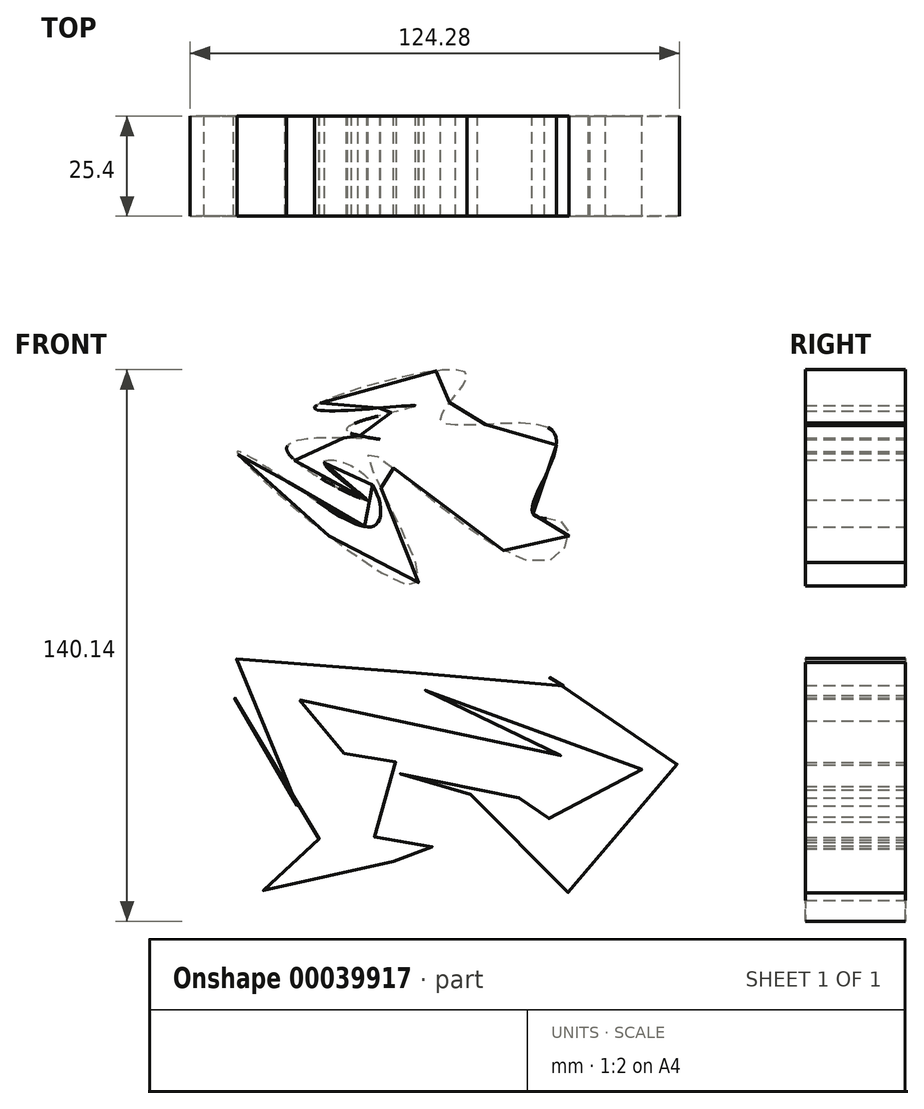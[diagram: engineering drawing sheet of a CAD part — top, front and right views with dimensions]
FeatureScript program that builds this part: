
annotation { "Feature Type Name" : "Feature", "Feature Type Description" : "" }
export const myFeature = defineFeature(function(context is Context, id is Id, definition is map)
    precondition{}
    {
        {
            var Q0;
            Q0=qCreatedBy(makeId("Front.planeOp"),FACE);
            var sketch = newSketch(context, id + "F0", { "sketchPlane" : qUnion([Q0])});
            skFitSpline(sketch, "E0", {"points": [v(-55.23, 44.33) * mm, v(-9.72, 11.43) * mm, v(-22.11, 44.33) * mm, v(21.26, 16.98) * mm, v(28.1, 26.6) * mm, v(19.55, 29.59) * mm, v(24.89, 50.1) * mm, v(-3.74, 53.1) * mm, v(2.67, 65.05) * mm, v(-35.79, 56.08) * mm, v(-10.15, 56.72) * mm, v(-27.67, 50.74) * mm, v(-19.12, 48.18) * mm, v(-42.84, 46.25) * mm, v(-22.54, 32.8) * mm, v(-33.22, 41.98) * mm, v(-23.4, 39.42) * mm, v(-20.4, 26.39) * mm, v(-45.4, 39.42) * mm, v(-55.23, 44.33) * mm]});
            skSolve(sketch);
        }
        {
            var Q0;
            Q0=makeQuery(id+"F0.imprint","IMPRINT",FACE,{"disambiguationData":[TD([[makeQuery(id+"F0.imprint","IMPRINT",EDGE,{"derivedFrom":sQuery(id+"F0.wireOp",EDGE,"E0")}),1.0]])]});
            extrude(context, id + "F1", {"entities" : qUnion([Q0]), "depth" : 25.4 * mm});
        }
        {
            var Q0;
            Q0=qCreatedBy(makeId("Front.planeOp"),FACE);
            var sketch = newSketch(context, id + "F2", { "sketchPlane" : qUnion([Q0])});
            skFitSpline(sketch, "E1", {"points": [v(-39.63, -18.05) * mm, v(34.08, -34.5) * mm, v(-8.01, -16.56) * mm, v(44.54, -28.52) * mm, v(33, -55.44) * mm, v(22.97, -49.25) * mm, v(38.14, -40.06) * mm, v(9.93, -42.2) * mm, v(4.17, -35.14) * mm, v(-15.49, -38.35) * mm, v(-7.8, -44.97) * mm, v(2.88, -40.91) * mm, v(6.09, -52.24) * mm, v(26.81, -66.98) * mm, v(55.44, -47.1) * mm, v(50.53, -23.18) * mm, v(25.74, -12.71) * mm, v(5.88, -8.65) * mm, v(33.65, -16.56) * mm, v(-14, -10.58) * mm, v(-36.64, -8.44) * mm, v(-67.4, -13.78) * mm, v(-34.72, -47.54) * mm, v(-56.3, -17.63) * mm, v(-27.67, -49.89) * mm, v(-63.56, -54.16) * mm, v(-33.65, -68.47) * mm, v(-18.9, -54.37) * mm, v(-9.72, -74.24) * mm, v(-6.94, -55.87) * mm, v(0, -55.87) * mm, v(-14.63, -49.03) * mm, v(-23.82, -55.65) * mm, v(-21.68, -40.49) * mm, v(-15.28, -31.73) * mm, v(-34.5, -23.82) * mm, v(-26.39, -34.08) * mm, v(-41.13, -25.96) * mm, v(-39.63, -18.05) * mm]});
            skSolve(sketch);
        }
        {
            var Q0;
            Q0=makeQuery(id+"F2.imprint","IMPRINT",FACE,{"disambiguationData":[TD([[makeQuery(id+"F2.imprint","IMPRINT",EDGE,{"derivedFrom":sQuery(id+"F2.wireOp",EDGE,"E1")}),1.0]])]});
            extrude(context, id + "F3", {"entities" : qUnion([Q0]), "depth" : 25.4 * mm});
        }
    });
